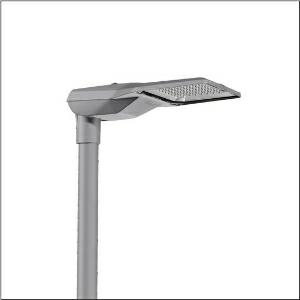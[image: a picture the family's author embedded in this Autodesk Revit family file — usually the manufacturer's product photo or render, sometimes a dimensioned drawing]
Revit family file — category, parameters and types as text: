
# Revit family: streetlight_sl_21_midi___st1_0a_5xe3d33s08nb_54c0
name_source: partatom
category: Lighting Fixtures
units: mm (PartAtom-declared; Revit-internal decimal feet)

## family parameters
Cut with Voids When Loaded = No
Host = Face
Light Source = No
Part Type = Normal
Room Calculation Point = No
Round Connector Dimension = Use Diameter
Shared = No

## types (1)
- --- (1 x LED, 22700 lm, 151.2 W, 3000K)
    Apparent Load = 151 VA
    CIE Flux Codes = 40 73 97 100 100
    Color Rendering = 70
    Color Temperature = 3000K
    Default Elevation = 1800 mm
    Description = Streetlight SL 21 midi, mast luminaire, primary light control with lens, of PMMA, primary optical cover: cover, of toughened safety glass, transparent, light distribution: ST1.0a, light emission: direct distribution, primary light characteristic: asymmetric, installation type: side-entry, post-top, LED, High Power LED, rated luminous flux: 22.700lm, luminous efficacy: 150lm/W, light colour: 730, colour temperature: 3000K, control gear: D4i, control: flexible luminous flux parameterisation, time-dependent luminous flux control, constant luminous flux control, overheat protection, pre-setting: logarithmic dimming characteristic, mains connection: 230..240V, AC, 50/60Hz, start of lifetime: 151W, end of service life: 157W, reduction: 70W, luminaire housing, of diecast aluminium, powder-coated, Siteco® metallic grey (DB 702S), corrosivity category C5 mid according to DIN EN ISO 12944, please order mast flange separately, inclination adjustable: 0°, 5°, 10°, 15°, sealing non-destructively replaceable, multi-level sealing system, length: 644mm, width: 335mm, height: 110mm, mast flange for spigot size: 42mm (side-entry): 5XC10008XM4, 60/48mm (side-entry/post-top): 5XC10108XM2, 76/60mm (side-entry/post-top): 5XC10108XM1, mounting height: 4..8m, Smart Interface above, protection rating (complete): IP66, insulation class (complete): insulation class II (safety insulation), certification: CE, ENEC, ENEC+, VDE, impact resistance: IK10, permissible operating ambient temperature for outdoor applications: -40..+50°C, standard-compliant lighting for roads and squares, packaging unit: 1 piece

Light Distribution: ST1.0a
    Height = 111 mm
    Lamp = 1 x LED
    Lamp Light Flux = 22700 lm
    Lamp Power = 151.2 W
    Lamp count = 1
    Length = 644 mm
    Luminous efficacy = 150 lm/W
    Manufacturer = Siteco
    ModVariant = No
    Model = 5XE3D33S08NB
    Number of Poles = 1
    OnlyDefault = Yes
    Power Factor = 1
    Product Name = Streetlight SL 21 midi | ST1.0a
    Product group = mast luminaire | pylon top
    ProductGroupID = 6100
    Protection Class = Protection class II
    Protection Degree = IP 66
    RLX_Detail_Level = 1
    RLX_Emergency_Light_Flux = 0 lm
    RLX_Emergency_Type = 0
    RLX_Emergency_Type_DB = No
    RlxData = <blob elided: 26973 chars, md5=0642419e>
    Socket = socket
    Standby Power = 0 W
    System Light Flux = 22700 lm
    System Power = 151 W
    Type Comments = factory setting: luminous flux: 100 % | dim-lin: 254 | 802 mA
    Type Image = l_1004302.jpg
    URL = http://relux.com
    VarID = @adj_170614
    Voltage = 0 V
    Weight = 0.00 kg
    Width = 336 mm

## geometry (parser evidence)
native form markers: Blend x4, Sweep x10
no freeform markers — native parametric forms only
